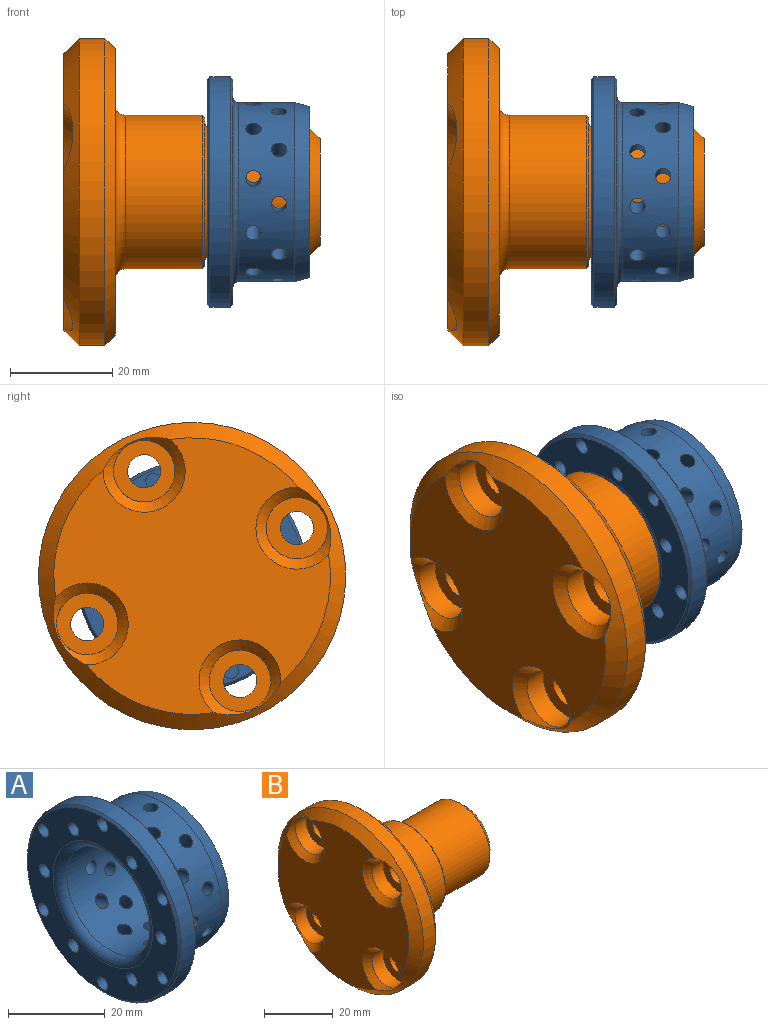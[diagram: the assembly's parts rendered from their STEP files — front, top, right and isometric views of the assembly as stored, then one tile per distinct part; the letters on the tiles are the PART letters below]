
ASSEMBLY  parts=2 mates=1
PART A: 56 faces, bbox 20x45x45 mm
  f0: cylinder r=12.5mm len=25mm, axis (-1,0,0), area 1187.6mm2, adj f6,f8,f36,f37,f38,f39,f40,f41
  f1: cylinder r=17.5mm len=35mm, axis (-1,0,0), area 1066.7mm2, adj f7,f11,f36,f37,f38,f39,f40,f41
  f2: plane 33.4x33.4mm, normal (1,0,0), area 303.7mm2, adj f6,f11
  f3: cylinder r=22.5mm len=45mm, axis (1,0,0), area 565.5mm2, adj f9,f10
  f4: plane 44x44mm, normal (-1,0,0), area 775.2mm2, adj f8,f10,f12,f14,f16,f18,f20,f22
  f5: plane 44x44mm, normal (1,0,0), area 445.3mm2, adj f7,f9
  f6: torus R=13.5mm, axis (-1,0,0), area 127mm2, adj f0,f2
  f7: torus R=18.5mm, axis (-1,0,0), area 176.3mm2, adj f1,f5
  f8: torus R=14.5mm, axis (-1,0,0), area 261.1mm2, adj f0,f4
  f9: cone r=22.5mm half-angle=45deg, axis (-1,0,0), area 98.9mm2, adj f3,f5
  f10: cone r=22mm half-angle=45deg, axis (1,0,0), area 98.9mm2, adj f3,f4
  f11: cone r=17.5mm half-angle=14.9deg, axis (-1,0,0), area 333.6mm2, adj f1,f2
  f12: cylinder r=1.5mm len=4mm, axis (-1,0,0), area 37.7mm2, adj f4,f13
  f13: plane 3x3mm, normal (-1,0,0), area 7.1mm2, adj f12
  f14: cylinder r=1.5mm len=4mm, axis (-1,0,0), area 37.7mm2, adj f4,f15
  f15: plane 3x3mm, normal (-1,0,0), area 7.1mm2, adj f14
  f16: cylinder r=1.5mm len=4mm, axis (-1,0,0), area 37.7mm2, adj f4,f17
  f17: plane 3x3mm, normal (-1,0,0), area 7.1mm2, adj f16
  f18: cylinder r=1.5mm len=4mm, axis (-1,0,0), area 37.7mm2, adj f4,f19
  f19: plane 3x3mm, normal (-1,0,0), area 7.1mm2, adj f18
  f20: cylinder r=1.5mm len=4mm, axis (-1,0,0), area 37.7mm2, adj f4,f21
  f21: plane 3x3mm, normal (-1,0,0), area 7.1mm2, adj f20
  f22: cylinder r=1.5mm len=4mm, axis (-1,0,0), area 37.7mm2, adj f4,f23
  f23: plane 3x3mm, normal (-1,0,0), area 7.1mm2, adj f22
  f24: cylinder r=1.5mm len=4mm, axis (-1,0,0), area 37.7mm2, adj f4,f25
  f25: plane 3x3mm, normal (-1,0,0), area 7.1mm2, adj f24
  f26: cylinder r=1.5mm len=4mm, axis (-1,0,0), area 37.7mm2, adj f4,f27
  f27: plane 3x3mm, normal (-1,0,0), area 7.1mm2, adj f26
  f28: cylinder r=1.5mm len=4mm, axis (-1,0,0), area 37.7mm2, adj f4,f29
  f29: plane 3x3mm, normal (-1,0,0), area 7.1mm2, adj f28
  f30: cylinder r=1.5mm len=4mm, axis (-1,0,0), area 37.7mm2, adj f4,f31
  f31: plane 3x3mm, normal (-1,0,0), area 7.1mm2, adj f30
  f32: cylinder r=1.5mm len=4mm, axis (-1,0,0), area 37.7mm2, adj f4,f33
  f33: plane 3x3mm, normal (-1,0,0), area 7.1mm2, adj f32
  f34: cylinder r=1.5mm len=4mm, axis (-1,0,0), area 37.7mm2, adj f4,f35
  f35: plane 3x3mm, normal (-1,0,0), area 7.1mm2, adj f34
  f36: cylinder r=1.5mm len=6.47mm, axis (0,0,1), area 50.3mm2, adj f0,f1
  f37: cylinder r=1.5mm len=5.09mm, axis (0,0,1), area 47.3mm2, adj f0,f1
  f38: cylinder r=1.5mm len=7mm, axis (0,-0.59,0.81), area 50.3mm2, adj f0,f1
  f39: cylinder r=1.5mm len=5.88mm, axis (0,-0.59,0.81), area 47.3mm2, adj f0,f1
  f40: cylinder r=1.5mm len=7.08mm, axis (0,-0.95,0.31), area 50.3mm2, adj f0,f1
  f41: cylinder r=1.5mm len=5.77mm, axis (0,-0.95,0.31), area 47.3mm2, adj f0,f1
  f42: cylinder r=1.5mm len=7.08mm, axis (0,-0.95,-0.31), area 50.3mm2, adj f0,f1
  f43: cylinder r=1.5mm len=5.77mm, axis (0,-0.95,-0.31), area 47.3mm2, adj f0,f1
  f44: cylinder r=1.5mm len=7mm, axis (0,-0.59,-0.81), area 50.3mm2, adj f0,f1
  f45: cylinder r=1.5mm len=5.88mm, axis (0,-0.59,-0.81), area 47.3mm2, adj f0,f1
  f46: cylinder r=1.5mm len=6.47mm, axis (0,0,-1), area 50.3mm2, adj f0,f1
  f47: cylinder r=1.5mm len=5.09mm, axis (0,0,-1), area 47.3mm2, adj f0,f1
  f48: cylinder r=1.5mm len=7mm, axis (0,0.59,-0.81), area 50.3mm2, adj f0,f1
  f49: cylinder r=1.5mm len=5.88mm, axis (0,0.59,-0.81), area 47.3mm2, adj f0,f1
  f50: cylinder r=1.5mm len=7.08mm, axis (0,0.95,-0.31), area 50.3mm2, adj f0,f1
  f51: cylinder r=1.5mm len=5.77mm, axis (0,0.95,-0.31), area 47.3mm2, adj f0,f1
  f52: cylinder r=1.5mm len=7.08mm, axis (0,0.95,0.31), area 50.3mm2, adj f0,f1
  f53: cylinder r=1.5mm len=5.77mm, axis (0,0.95,0.31), area 47.3mm2, adj f0,f1
  f54: cylinder r=1.5mm len=7mm, axis (0,0.59,0.81), area 50.3mm2, adj f0,f1
  f55: cylinder r=1.5mm len=5.88mm, axis (0,0.59,0.81), area 47.3mm2, adj f0,f1
PART B: 29 faces, bbox 50x60x60 mm
  f0: cone r=30mm half-angle=45deg, axis (1,0,0), area 662.9mm2, adj f2,f3,f25,f26,f27,f28
  f1: plane 56x56mm, normal (1,0,0), area 1422.4mm2, adj f8,f9,f13,f16,f19,f22
  f2: cylinder r=30mm len=60mm, axis (1,0,0), area 942.5mm2, adj f0,f9
  f3: plane 54x54mm, normal (-1,0,0), area 1632.5mm2, adj f0,f25,f26,f27,f28
  f4: cylinder r=15mm len=30mm, axis (1,0,0), area 1413.7mm2, adj f8,f10
  f5: plane 29x29mm, normal (1,0,0), area 88mm2, adj f10,f11
  f6: plane 21x21mm, normal (1,0,0), area 346.4mm2, adj f12
  f7: cylinder r=12.5mm len=25mm, axis (-1,0,0), area 1531.5mm2, adj f11,f12
  f8: torus R=17mm, axis (1,0,0), area 310.4mm2, adj f1,f4
  f9: cone r=28mm half-angle=45deg, axis (-1,0,0), area 515.4mm2, adj f1,f2
  f10: cone r=14.5mm half-angle=45deg, axis (-1,0,0), area 65.5mm2, adj f4,f5
  f11: torus R=13.5mm, axis (1,0,0), area 127mm2, adj f5,f7
  f12: cone r=10.5mm half-angle=45deg, axis (-1,0,0), area 204.4mm2, adj f6,f7
  f13: cylinder r=3.25mm len=6.5mm, axis (-1,0,0), area 71.5mm2, adj f1,f14
  f14: plane 12x12mm, normal (-1,0,0), area 79.9mm2, adj f13,f15
  f15: cylinder r=6mm len=12mm, axis (-1,0,0), area 169.6mm2, adj f14,f28
  f16: cylinder r=3.25mm len=6.5mm, axis (-1,0,0), area 71.5mm2, adj f1,f17
  f17: plane 12x12mm, normal (-1,0,0), area 79.9mm2, adj f16,f18
  f18: cylinder r=6mm len=12mm, axis (-1,0,0), area 169.6mm2, adj f17,f27
  f19: cylinder r=3.25mm len=6.5mm, axis (-1,0,0), area 71.5mm2, adj f1,f20
  f20: plane 12x12mm, normal (-1,0,0), area 79.9mm2, adj f19,f21
  f21: cylinder r=6mm len=12mm, axis (-1,0,0), area 169.6mm2, adj f20,f26
  f22: cylinder r=3.25mm len=6.5mm, axis (-1,0,0), area 71.5mm2, adj f1,f23
  f23: plane 12x12mm, normal (-1,0,0), area 79.9mm2, adj f22,f24
  f24: cylinder r=6mm len=12mm, axis (-1,0,0), area 169.6mm2, adj f23,f25
  f25: cone r=6mm half-angle=45deg, axis (-1,0,0), area 96.9mm2, adj f0,f3,f24
  f26: cone r=6mm half-angle=45deg, axis (-1,0,0), area 96.9mm2, adj f0,f3,f21
  f27: cone r=6mm half-angle=45deg, axis (-1,0,0), area 96.9mm2, adj f0,f3,f18
  f28: cone r=6mm half-angle=45deg, axis (-1,0,0), area 96.9mm2, adj f0,f3,f15
PLACE A rot(axis=(-1,0,0),82.2deg) t=(-20.05,-17.69,-20.85)mm fixed
PLACE B rot(axis=(1,0,0),110.4deg) t=(-20.05,-17.69,-20.85)mm
MATE revolute B.f0 <-> A.f0  axis (1,0,0) through (-36.8,-17.69,-20.85)mm
